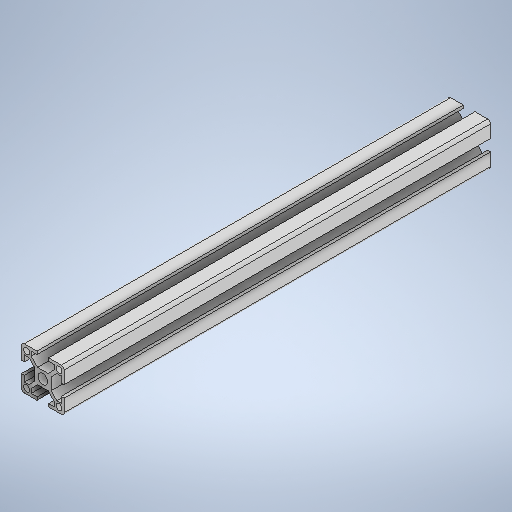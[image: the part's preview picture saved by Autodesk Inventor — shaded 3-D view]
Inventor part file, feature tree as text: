
AUTODESK INVENTOR PART (.ipt)
format: ipt  version: 2025 (Build 290162000, 162)  size: 307,712 bytes
history: native  units: in
note: dims shown in document units (in); Inventor stores cm internally (conversion verified against a paired STEP export)
features: extrude x1, sketch x1
ambient origin geometry x8: Origin, YZ Plane, XZ Plane, XY Plane, X Axis, Y Axis, Z Axis, Center Point
bodies: Solid1 (feature_tree)
feature tree (2):
  extrude  "Extrusion1"  Depth=11.811in
  sketch  "Sketch1"  dims[d6=11.811in d7=0.0in d8=0.1969in d9=0.0344in]
